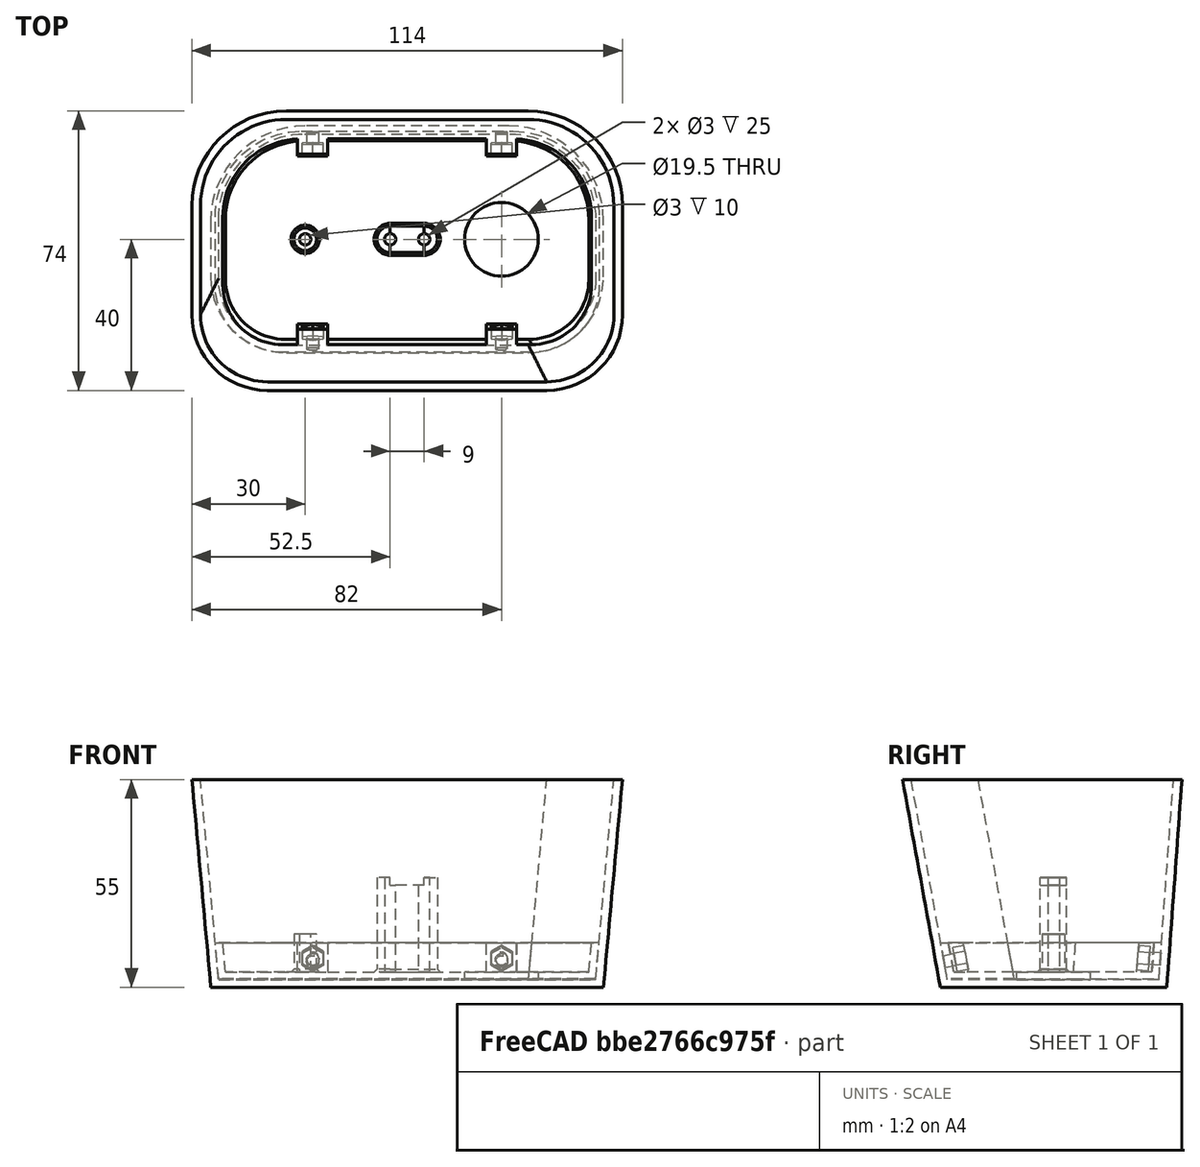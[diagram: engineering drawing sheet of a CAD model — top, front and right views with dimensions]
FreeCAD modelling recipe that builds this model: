
FCSTD DOCUMENT  (FreeCAD 0.19R22894 (Git))
Label: Rear_Cover_Plate
License: All rights reserved
LicenseURL: http://en.wikipedia.org/wiki/All_rights_reserved
objects: Sketcher::SketchObject×15, PartDesign::Pocket×7, PartDesign::Pad×4, PartDesign::AdditiveLoft×2, PartDesign::Thickness×2, PartDesign::Body×2, PartDesign::Chamfer×2, PartDesign::Boolean×1
note: 52 computed .brp shape members not serialized (recipe doc carries the construction recipe); baked Part::Feature solids carry a one-line shape summary decoded from their .brp

FEATURE [Sketcher::SketchObject] Sketch090
  MapMode = 5
  Support = -> [XY_Plane047]
  sketch-geometry (8):
    g0: LineSegment StartX=25 StartY=10 StartZ=0 EndX=89 EndY=10 EndZ=0
    g1: LineSegment StartX=109 StartY=30 StartZ=0 EndX=109 EndY=45 EndZ=0
    g2: LineSegment StartX=84 StartY=70 StartZ=0 EndX=30 EndY=70 EndZ=0
    g3: LineSegment StartX=5 StartY=45 StartZ=0 EndX=5 EndY=30 EndZ=0
    g4: ArcOfCircle CenterX=30 CenterY=45 CenterZ=0 NormalX=0 NormalY=0 NormalZ=1 AngleXU=0 Radius=25 StartAngle=1.5708 EndAngle=3.14159
    g5: ArcOfCircle CenterX=84 CenterY=45 CenterZ=0 NormalX=0 NormalY=0 NormalZ=1 AngleXU=0 Radius=25 StartAngle=0 EndAngle=1.5708
    g6: ArcOfCircle CenterX=89 CenterY=30 CenterZ=0 NormalX=0 NormalY=0 NormalZ=1 AngleXU=0 Radius=20 StartAngle=4.71239 EndAngle=6.28319
    g7: ArcOfCircle CenterX=25 CenterY=30 CenterZ=0 NormalX=0 NormalY=0 NormalZ=1 AngleXU=0 Radius=20 StartAngle=3.14159 EndAngle=4.71239
  constraints (20):
    c: Horizontal(g0)
    c: Horizontal(g2)
    c: Vertical(g1)
    c: Vertical(g3)
    c: Tangent(g3,g4) = -1.5708
    c: Tangent(g2,g4) = -1.5708
    c: Tangent(g2,g5) = -1.5708
    c: Tangent(g1,g5) = -1.5708
    c: Tangent(g1,g6) = -1.5708
    c: Tangent(g0,g6) = -1.5708
    c: Tangent(g0,g7) = -1.5708
    c: Tangent(g3,g7) = -1.5708
    c: Equal(g4,g5)
    c: Equal(g7,g6)
    c: Radius(g5) = 25
    c: Radius(g6) = 20
    c: DistanceY(g0,g2) = 60
    c: DistanceX(g3,g1) = 104
    c: DistanceY(g-1,g0) = 10
    c: DistanceX(g-1,g3) = 5
FEATURE [Sketcher::SketchObject] Sketch093
  AttachmentOffset = pos=(0,0,55) rot=(0,0,1;0rad)
  MapMode = 5
  Placement = pos=(0,0,55) rot=(0,0,1;0rad)
  Support = -> [XY_Plane048]
  sketch-geometry (8):
    g0: LineSegment StartX=25 StartY=74 StartZ=0 EndX=89 EndY=74 EndZ=0
    g1: LineSegment StartX=114 StartY=49 StartZ=0 EndX=114 EndY=20 EndZ=0
    g2: LineSegment StartX=94 StartY=0 StartZ=0 EndX=20 EndY=0 EndZ=0
    g3: LineSegment StartX=0 StartY=20 StartZ=0 EndX=0 EndY=49 EndZ=0
    g4: ArcOfCircle CenterX=20 CenterY=20 CenterZ=0 NormalX=0 NormalY=0 NormalZ=1 AngleXU=0 Radius=20 StartAngle=3.14159 EndAngle=4.71239
    g5: ArcOfCircle CenterX=25 CenterY=49 CenterZ=0 NormalX=0 NormalY=0 NormalZ=1 AngleXU=0 Radius=25 StartAngle=1.5708 EndAngle=3.14159
    g6: ArcOfCircle CenterX=89 CenterY=49 CenterZ=0 NormalX=0 NormalY=0 NormalZ=1 AngleXU=0 Radius=25 StartAngle=0 EndAngle=1.5708
    g7: ArcOfCircle CenterX=94 CenterY=20 CenterZ=0 NormalX=0 NormalY=0 NormalZ=1 AngleXU=0 Radius=20 StartAngle=4.71239 EndAngle=6.28319
  constraints (20):
    c: Horizontal(g0)
    c: Horizontal(g2)
    c: Vertical(g1)
    c: Vertical(g3)
    c: Tangent(g2,g4) = 1.5708
    c: Tangent(g3,g4) = 1.5708
    c: Tangent(g3,g5) = 1.5708
    c: Tangent(g0,g5) = 1.5708
    c: Tangent(g0,g6) = 1.5708
    c: Tangent(g1,g6) = 1.5708
    c: Tangent(g1,g7) = 1.5708
    c: Tangent(g2,g7) = 1.5708
    c: Equal(g4,g7)
    c: Equal(g5,g6)
    c: Radius(g6) = 25
    c: Radius(g7) = 20
    c: PointOnObject(g2,g-1)
    c: PointOnObject(g3,g-2)
    c: DistanceX(g3,g1) = 114
    c: DistanceY(g2,g0) = 74
FEATURE [Sketcher::SketchObject] Sketch094
  MapMode = 5
  Support = -> [XY_Plane048]
  sketch-geometry (8):
    g0: LineSegment StartX=25 StartY=10 StartZ=0 EndX=89 EndY=10 EndZ=0
    g1: LineSegment StartX=109 StartY=30 StartZ=0 EndX=109 EndY=45 EndZ=0
    g2: LineSegment StartX=84 StartY=70 StartZ=0 EndX=30 EndY=70 EndZ=0
    g3: LineSegment StartX=5 StartY=45 StartZ=0 EndX=5 EndY=30 EndZ=0
    g4: ArcOfCircle CenterX=30 CenterY=45 CenterZ=0 NormalX=0 NormalY=0 NormalZ=1 AngleXU=0 Radius=25 StartAngle=1.5708 EndAngle=3.14159
    g5: ArcOfCircle CenterX=84 CenterY=45 CenterZ=0 NormalX=0 NormalY=0 NormalZ=1 AngleXU=0 Radius=25 StartAngle=0 EndAngle=1.5708
    g6: ArcOfCircle CenterX=89 CenterY=30 CenterZ=0 NormalX=0 NormalY=0 NormalZ=1 AngleXU=0 Radius=20 StartAngle=4.71239 EndAngle=6.28319
    g7: ArcOfCircle CenterX=25 CenterY=30 CenterZ=0 NormalX=0 NormalY=0 NormalZ=1 AngleXU=0 Radius=20 StartAngle=3.14159 EndAngle=4.71239
  constraints (20):
    c: Horizontal(g0)
    c: Horizontal(g2)
    c: Vertical(g1)
    c: Vertical(g3)
    c: Tangent(g3,g4) = -1.5708
    c: Tangent(g2,g4) = -1.5708
    c: Tangent(g2,g5) = -1.5708
    c: Tangent(g1,g5) = -1.5708
    c: Tangent(g1,g6) = -1.5708
    c: Tangent(g0,g6) = -1.5708
    c: Tangent(g0,g7) = -1.5708
    c: Tangent(g3,g7) = -1.5708
    c: Equal(g4,g5)
    c: Equal(g7,g6)
    c: Radius(g5) = 25
    c: Radius(g6) = 20
    c: DistanceY(g0,g2) = 60
    c: DistanceX(g3,g1) = 104
    c: DistanceY(g-1,g0) = 10
    c: DistanceX(g-1,g3) = 5
FEATURE [PartDesign::AdditiveLoft] AdditiveLoft002  label="Baseplate001"
  AllowMultiFace = false
  Closed = false
  Profile = -> Sketch094
  Ruled = false
  Sections = -> [Sketch093]
FEATURE [PartDesign::Thickness] Thickness002  label="Make Shell"
  Base = -> AdditiveLoft002 [Face3]
  BaseFeature = -> AdditiveLoft002
  Intersection = false
  Join = 0
  Mode = 0
  Reversed = true
  SupportTransform = false
  Value = 2.25
FEATURE [PartDesign::Body] Body033  label="Rear_Cover_long"
  Group = -> [Sketch093,Sketch094,AdditiveLoft002,Thickness002]
  Origin = -> Origin049
  Tip = -> Thickness002
FEATURE [Sketcher::SketchObject] Sketch092
  AttachmentOffset = pos=(0,0,55) rot=(0,0,1;0rad)
  MapMode = 5
  Placement = pos=(0,0,55) rot=(0,0,1;0rad)
  Support = -> [XY_Plane047]
  sketch-geometry (8):
    g0: LineSegment StartX=25 StartY=74 StartZ=0 EndX=89 EndY=74 EndZ=0
    g1: LineSegment StartX=114 StartY=49 StartZ=0 EndX=114 EndY=20 EndZ=0
    g2: LineSegment StartX=94 StartY=0 StartZ=0 EndX=20 EndY=0 EndZ=0
    g3: LineSegment StartX=0 StartY=20 StartZ=0 EndX=0 EndY=49 EndZ=0
    g4: ArcOfCircle CenterX=20 CenterY=20 CenterZ=0 NormalX=0 NormalY=0 NormalZ=1 AngleXU=0 Radius=20 StartAngle=3.14159 EndAngle=4.71239
    g5: ArcOfCircle CenterX=25 CenterY=49 CenterZ=0 NormalX=0 NormalY=0 NormalZ=1 AngleXU=0 Radius=25 StartAngle=1.5708 EndAngle=3.14159
    g6: ArcOfCircle CenterX=89 CenterY=49 CenterZ=0 NormalX=0 NormalY=0 NormalZ=1 AngleXU=0 Radius=25 StartAngle=0 EndAngle=1.5708
    g7: ArcOfCircle CenterX=94 CenterY=20 CenterZ=0 NormalX=0 NormalY=0 NormalZ=1 AngleXU=0 Radius=20 StartAngle=4.71239 EndAngle=6.28319
  constraints (20):
    c: Horizontal(g0)
    c: Horizontal(g2)
    c: Vertical(g1)
    c: Vertical(g3)
    c: Tangent(g2,g4) = 1.5708
    c: Tangent(g3,g4) = 1.5708
    c: Tangent(g3,g5) = 1.5708
    c: Tangent(g0,g5) = 1.5708
    c: Tangent(g0,g6) = 1.5708
    c: Tangent(g1,g6) = 1.5708
    c: Tangent(g1,g7) = 1.5708
    c: Tangent(g2,g7) = 1.5708
    c: Equal(g4,g7)
    c: Equal(g5,g6)
    c: Radius(g6) = 25
    c: Radius(g7) = 20
    c: PointOnObject(g2,g-1)
    c: PointOnObject(g3,g-2)
    c: DistanceX(g3,g1) = 114
    c: DistanceY(g2,g0) = 74
FEATURE [PartDesign::AdditiveLoft] AdditiveLoft001  label="Baseplate"
  AllowMultiFace = false
  Closed = false
  Profile = -> Sketch090
  Ruled = false
  Sections = -> [Sketch092]
FEATURE [PartDesign::Thickness] Thickness001  label="Make Thick Shell"
  Base = -> AdditiveLoft001 [Face3]
  BaseFeature = -> AdditiveLoft001
  Intersection = false
  Join = 0
  Mode = 0
  Reversed = true
  SupportTransform = false
  Value = 4.25
FEATURE [PartDesign::Boolean] Boolean
  BaseFeature = -> Thickness001
  Group = -> [Body033]
  Type = 1
FEATURE [Sketcher::SketchObject] Sketch095
  MapMode = 5
  Placement = pos=(0,0,55) rot=(0,0,1;0rad)
  Support = -> [Boolean]
  sketch-geometry (4):
    g0: LineSegment StartX=0 StartY=0 StartZ=0 EndX=118 EndY=0 EndZ=0
    g1: LineSegment StartX=118 StartY=0 StartZ=0 EndX=118 EndY=75 EndZ=0
    g2: LineSegment StartX=118 StartY=75 StartZ=0 EndX=0 EndY=75 EndZ=0
    g3: LineSegment StartX=0 StartY=75 StartZ=0 EndX=0 EndY=0 EndZ=0
  constraints (11):
    c: Coincident(g0,g1)
    c: Coincident(g1,g2)
    c: Coincident(g2,g3)
    c: Coincident(g3,g0)
    c: Horizontal(g0)
    c: Horizontal(g2)
    c: Vertical(g1)
    c: Vertical(g3)
    c: Coincident(g0,g-1)
    c: DistanceX(g2,g2) = 118
    c: DistanceY(g1,g1) = 75
FEATURE [PartDesign::Pocket] Pocket033  label="Shorten Shell"
  AllowMultiFace = false
  BaseFeature = -> Boolean
  Length = 43
  Length2 = 100
  Profile = -> Sketch095
  Type = 0
FEATURE [Sketcher::SketchObject] Sketch254
  AttachmentOffset = pos=(0,0,32) rot=(0,0,1;0rad)
  ExternalGeometry = -> [Pocket033]
  MapMode = 5
  Placement = pos=(32,-7.1e-15,7.1e-15) rot=(0.57735,0.57735,0.57735;2.0944rad)
  Support = -> [YZ_Plane047]
  sketch-geometry (8):
    g0: LineSegment StartX=12.1379 StartY=12 StartZ=0 EndX=13.5469 EndY=4.25 EndZ=0
    g1: LineSegment StartX=13.5469 StartY=4.25 StartZ=0 EndX=17.5469 EndY=4.25 EndZ=0
    g2: LineSegment StartX=17.5469 StartY=4.25 StartZ=0 EndX=16.1379 EndY=12 EndZ=0
    g3: LineSegment StartX=16.1379 StartY=12 StartZ=0 EndX=12.1379 EndY=12 EndZ=0
    g4: LineSegment StartX=66.0479 StartY=4.25 StartZ=0 EndX=62.0479 EndY=4.25 EndZ=0
    g5: LineSegment StartX=62.0479 StartY=4.25 StartZ=0 EndX=62.6115 EndY=12 EndZ=0
    g6: LineSegment StartX=62.6115 StartY=12 StartZ=0 EndX=66.6115 EndY=12 EndZ=0
    g7: LineSegment StartX=66.6115 StartY=12 StartZ=0 EndX=66.0479 EndY=4.25 EndZ=0
  constraints (20):
    c: Coincident(g0,g-3)
    c: Coincident(g0,g-3)
    c: Coincident(g0,g1)
    c: Horizontal(g1)
    c: Coincident(g1,g2)
    c: Coincident(g2,g3)
    c: Horizontal(g3)
    c: Coincident(g3,g0)
    c: Parallel(g2,g0)
    c: DistanceX(g3,g3) = 4
    c: Horizontal(g4)
    c: Coincident(g4,g5)
    c: Coincident(g5,g6)
    c: Coincident(g6,g-4)
    c: Horizontal(g6)
    c: Coincident(g6,g7)
    c: Coincident(g7,g4)
    c: Parallel(g7,g5)
    c: Coincident(g4,g-4)
    c: DistanceX(g6,g6) = 4
FEATURE [PartDesign::Pad] Pad112  label="Add Screwpads right"
  AllowMultiFace = false
  BaseFeature = -> Pocket033
  Direction = (1,1,1)
  Length = 4
  Length2 = 4
  Profile = -> Sketch254
  Type = 4
FEATURE [Sketcher::SketchObject] Sketch255
  AttachmentOffset = pos=(0,0,82) rot=(0,0,1;0rad)
  ExternalGeometry = -> [Pocket033]
  MapMode = 5
  Placement = pos=(82,-1.82e-14,1.82e-14) rot=(0.57735,0.57735,0.57735;2.0944rad)
  Support = -> [YZ_Plane047]
  sketch-geometry (8):
    g0: LineSegment StartX=12.1379 StartY=12 StartZ=0 EndX=13.5469 EndY=4.25 EndZ=0
    g1: LineSegment StartX=13.5469 StartY=4.25 StartZ=0 EndX=17.5469 EndY=4.25 EndZ=0
    g2: LineSegment StartX=17.5469 StartY=4.25 StartZ=0 EndX=16.1379 EndY=12 EndZ=0
    g3: LineSegment StartX=16.1379 StartY=12 StartZ=0 EndX=12.1379 EndY=12 EndZ=0
    g4: LineSegment StartX=66.0479 StartY=4.25 StartZ=0 EndX=62.0479 EndY=4.25 EndZ=0
    g5: LineSegment StartX=62.0479 StartY=4.25 StartZ=0 EndX=62.6115 EndY=12 EndZ=0
    g6: LineSegment StartX=62.6115 StartY=12 StartZ=0 EndX=66.6115 EndY=12 EndZ=0
    g7: LineSegment StartX=66.6115 StartY=12 StartZ=0 EndX=66.0479 EndY=4.25 EndZ=0
  constraints (20):
    c: Coincident(g0,g-3)
    c: Coincident(g0,g-3)
    c: Coincident(g0,g1)
    c: Horizontal(g1)
    c: Coincident(g1,g2)
    c: Coincident(g2,g3)
    c: Horizontal(g3)
    c: Coincident(g3,g0)
    c: Parallel(g2,g0)
    c: DistanceX(g3,g3) = 4
    c: Horizontal(g4)
    c: Coincident(g4,g5)
    c: Coincident(g5,g6)
    c: Coincident(g6,g-4)
    c: Horizontal(g6)
    c: Coincident(g6,g7)
    c: Coincident(g7,g4)
    c: Parallel(g7,g5)
    c: Coincident(g4,g-4)
    c: DistanceX(g6,g6) = 4
FEATURE [PartDesign::Pad] Pad113  label="Add Screwpads left"
  AllowMultiFace = false
  BaseFeature = -> Pad112
  Direction = (1,1,1)
  Length = 4
  Length2 = 4
  Profile = -> Sketch255
  Type = 4
FEATURE [Sketcher::SketchObject] Sketch256
  ExternalGeometry = -> [Pad113]
  MapMode = 5
  Placement = pos=(3e-15,17.7334,3.22426) rot=(0,0.640747,0.767752;3.14159rad)
  Support = -> [Pad113]
  sketch-geometry (5):
    g0: Circle CenterX=-82 CenterY=4.98108 CenterZ=0 NormalX=0 NormalY=0 NormalZ=1 AngleXU=0 Radius=1.6
    g1: Circle CenterX=-32 CenterY=4.98108 CenterZ=0 NormalX=0 NormalY=0 NormalZ=1 AngleXU=0 Radius=1.6
    g2: LineSegment [constr] StartX=-86 StartY=8.91961 StartZ=0 EndX=-82 EndY=4.98108 EndZ=0
    g3: LineSegment [constr] StartX=-82 StartY=4.98108 StartZ=0 EndX=-78 EndY=8.91961 EndZ=0
    g4: LineSegment [constr] StartX=-78 StartY=1.04255 StartZ=0 EndX=-82 EndY=4.98108 EndZ=0
  constraints (12):
    c: Equal(g1,g0)
    c: Radius(g0) = 1.6
    c: Horizontal(g0,g1)
    c: DistanceX(g0,g1) = 50
    c: Coincident(g2,g-3)
    c: Coincident(g2,g0)
    c: Coincident(g3,g0)
    c: Coincident(g3,g-3)
    c: Equal(g2,g3)
    c: Coincident(g4,g-4)
    c: Coincident(g4,g0)
    c: Equal(g4,g3)
FEATURE [PartDesign::Pocket] Pocket115  label="Add Screwholes top"
  AllowMultiFace = false
  BaseFeature = -> Pad113
  Length = 10
  Length2 = 100
  Profile = -> Sketch256
  Type = 0
FEATURE [Sketcher::SketchObject] Sketch257
  ExternalGeometry = -> [Pocket115]
  MapMode = 5
  Placement = pos=(3e-15,17.7334,3.22426) rot=(0,0.640747,0.767752;3.14159rad)
  Support = -> [Pocket115]
  sketch-geometry (14):
    g0: LineSegment StartX=-82 StartY=8.21424 StartZ=0 EndX=-84.8 EndY=6.59766 EndZ=0
    g1: LineSegment StartX=-84.8 StartY=6.59766 StartZ=0 EndX=-84.8 EndY=3.3645 EndZ=0
    g2: LineSegment StartX=-84.8 StartY=3.3645 StartZ=0 EndX=-82 EndY=1.74792 EndZ=0
    g3: LineSegment StartX=-82 StartY=1.74792 StartZ=0 EndX=-79.2 EndY=3.3645 EndZ=0
    g4: LineSegment StartX=-79.2 StartY=3.3645 StartZ=0 EndX=-79.2 EndY=6.59766 EndZ=0
    g5: LineSegment StartX=-79.2 StartY=6.59766 StartZ=0 EndX=-82 EndY=8.21424 EndZ=0
    g6: Circle [constr] CenterX=-82 CenterY=4.98108 CenterZ=0 NormalX=0 NormalY=0 NormalZ=1 AngleXU=0 Radius=3.23316
    g7: LineSegment StartX=-32 StartY=8.21424 StartZ=0 EndX=-34.8 EndY=6.59766 EndZ=0
    g8: LineSegment StartX=-34.8 StartY=6.59766 StartZ=0 EndX=-34.8 EndY=3.3645 EndZ=0
    g9: LineSegment StartX=-34.8 StartY=3.3645 StartZ=0 EndX=-32 EndY=1.74792 EndZ=0
    g10: LineSegment StartX=-32 StartY=1.74792 StartZ=0 EndX=-29.2 EndY=3.3645 EndZ=0
    g11: LineSegment StartX=-29.2 StartY=3.3645 StartZ=0 EndX=-29.2 EndY=6.59766 EndZ=0
    g12: LineSegment StartX=-29.2 StartY=6.59766 StartZ=0 EndX=-32 EndY=8.21424 EndZ=0
    g13: Circle [constr] CenterX=-32 CenterY=4.98108 CenterZ=0 NormalX=0 NormalY=0 NormalZ=1 AngleXU=0 Radius=3.23316
  constraints (33):
    c: Coincident(g0,g1)
    c: Coincident(g1,g2)
    c: Coincident(g2,g3)
    c: Coincident(g3,g4)
    c: Coincident(g4,g5)
    c: Coincident(g5,g0)
    c: Equal(g0, g1-g5) x5
    c: PointOnObject(g0,g6)
    c: PointOnObject(g1,g6)
    c: PointOnObject(g2,g6)
    c: PointOnObject(g3,g6)
    c: PointOnObject(g4,g6)
    c: PointOnObject(g5,g6)
    c: Coincident(g7,g8)
    c: Coincident(g8,g9)
    c: Coincident(g9,g10)
    c: Coincident(g10,g11)
    c: Coincident(g11,g12)
    c: Coincident(g12,g7)
    c: Equal(g7, g8-g12) x5
    c: PointOnObject(g7,g13)
    c: PointOnObject(g8,g13)
    c: PointOnObject(g9,g13)
    c: PointOnObject(g10,g13)
    c: PointOnObject(g11,g13)
    c: PointOnObject(g12,g13)
    c: Coincident(g6,g-3)
    c: Vertical(g1)
    c: Vertical(g8)
    c: Equal(g6,g13)
    c: DistanceX(g0,g4) = 5.6
    c: Horizontal(g13,g6)
    c: DistanceX(g6,g13) = 50
FEATURE [PartDesign::Pocket] Pocket116  label="Add Screwholes bottom"
  AllowMultiFace = false
  BaseFeature = -> Pocket115
  Length = 3
  Length2 = 100
  Profile = -> Sketch257
  Type = 0
FEATURE [Sketcher::SketchObject] Sketch258
  ExternalGeometry = -> [Pocket116]
  MapMode = 5
  Placement = pos=(1.49e-14,61.4139,-4.46647) rot=(1,0,0;1.4982rad)
  Support = -> [Pocket116]
  sketch-geometry (5):
    g0: Circle CenterX=32 CenterY=12.6247 CenterZ=0 NormalX=0 NormalY=0 NormalZ=1 AngleXU=0 Radius=1.6
    g1: Circle CenterX=82 CenterY=12.6247 CenterZ=0 NormalX=0 NormalY=0 NormalZ=1 AngleXU=0 Radius=1.6
    g2: LineSegment [constr] StartX=28 StartY=16.51 StartZ=0 EndX=32 EndY=12.6247 EndZ=0
    g3: LineSegment [constr] StartX=32 StartY=12.6247 StartZ=0 EndX=36 EndY=16.51 EndZ=0
    g4: LineSegment [constr] StartX=32 StartY=12.6247 StartZ=0 EndX=36 EndY=8.73949 EndZ=0
  constraints (12):
    c: Horizontal(g0,g1)
    c: Equal(g1,g0)
    c: DistanceX(g0,g1) = 50
    c: Coincident(g2,g-3)
    c: Coincident(g2,g0)
    c: Coincident(g3,g0)
    c: Coincident(g3,g-3)
    c: Coincident(g4,g0)
    c: Coincident(g4,g-4)
    c: Equal(g2,g3)
    c: Equal(g3,g4)
    c: Radius(g0) = 1.6
FEATURE [PartDesign::Pocket] Pocket117  label="Add Nutpockets top"
  AllowMultiFace = false
  BaseFeature = -> Pocket116
  Length = 10
  Length2 = 100
  Profile = -> Sketch258
  Type = 0
FEATURE [Sketcher::SketchObject] Sketch259
  ExternalGeometry = -> [Pocket117]
  MapMode = 5
  Placement = pos=(1.49e-14,61.4139,-4.46647) rot=(1,0,0;1.4982rad)
  Support = -> [Pocket117]
  sketch-geometry (14):
    g0: LineSegment StartX=32 StartY=15.8579 StartZ=0 EndX=29.2 EndY=14.2413 EndZ=0
    g1: LineSegment StartX=29.2 StartY=14.2413 StartZ=0 EndX=29.2 EndY=11.0081 EndZ=0
    g2: LineSegment StartX=29.2 StartY=11.0081 StartZ=0 EndX=32 EndY=9.39156 EndZ=0
    g3: LineSegment StartX=32 StartY=9.39156 StartZ=0 EndX=34.8 EndY=11.0081 EndZ=0
    g4: LineSegment StartX=34.8 StartY=11.0081 StartZ=0 EndX=34.8 EndY=14.2413 EndZ=0
    g5: LineSegment StartX=34.8 StartY=14.2413 StartZ=0 EndX=32 EndY=15.8579 EndZ=0
    g6: Circle [constr] CenterX=32 CenterY=12.6247 CenterZ=0 NormalX=0 NormalY=0 NormalZ=1 AngleXU=0 Radius=3.23316
    g7: LineSegment StartX=82 StartY=15.8579 StartZ=0 EndX=79.2 EndY=14.2413 EndZ=0
    g8: LineSegment StartX=79.2 StartY=14.2413 StartZ=0 EndX=79.2 EndY=11.0081 EndZ=0
    g9: LineSegment StartX=79.2 StartY=11.0081 StartZ=0 EndX=82 EndY=9.39156 EndZ=0
    g10: LineSegment StartX=82 StartY=9.39156 StartZ=0 EndX=84.8 EndY=11.0081 EndZ=0
    g11: LineSegment StartX=84.8 StartY=11.0081 StartZ=0 EndX=84.8 EndY=14.2413 EndZ=0
    g12: LineSegment StartX=84.8 StartY=14.2413 StartZ=0 EndX=82 EndY=15.8579 EndZ=0
    g13: Circle [constr] CenterX=82 CenterY=12.6247 CenterZ=0 NormalX=0 NormalY=0 NormalZ=1 AngleXU=0 Radius=3.23316
  constraints (33):
    c: Coincident(g0,g1)
    c: Coincident(g1,g2)
    c: Coincident(g2,g3)
    c: Coincident(g3,g4)
    c: Coincident(g4,g5)
    c: Coincident(g5,g0)
    c: Equal(g0, g1-g5) x5
    c: PointOnObject(g0,g6)
    c: PointOnObject(g1,g6)
    c: PointOnObject(g2,g6)
    c: PointOnObject(g3,g6)
    c: PointOnObject(g4,g6)
    c: PointOnObject(g5,g6)
    c: Coincident(g7,g8)
    c: Coincident(g8,g9)
    c: Coincident(g9,g10)
    c: Coincident(g10,g11)
    c: Coincident(g11,g12)
    c: Coincident(g12,g7)
    c: Equal(g7, g8-g12) x5
    c: PointOnObject(g7,g13)
    c: PointOnObject(g8,g13)
    c: PointOnObject(g9,g13)
    c: PointOnObject(g10,g13)
    c: PointOnObject(g11,g13)
    c: PointOnObject(g12,g13)
    c: Vertical(g4)
    c: Vertical(g8)
    c: Equal(g13,g6)
    c: Coincident(g-3,g6)
    c: Horizontal(g6,g13)
    c: DistanceX(g6,g13) = 50
    c: DistanceX(g0,g4) = 5.6
FEATURE [PartDesign::Pocket] Pocket118  label="Add Nutpockets bottom"
  AllowMultiFace = false
  BaseFeature = -> Pocket117
  Length = 3
  Length2 = 100
  Profile = -> Sketch259
  Type = 0
FEATURE [Sketcher::SketchObject] Sketch660
  MapMode = 5
  Placement = pos=(0,0,4.25) rot=(0,0,1;0rad)
  Support = -> [Pocket118]
  sketch-geometry (2):
    g0: Circle CenterX=30 CenterY=40 CenterZ=0 NormalX=0 NormalY=0 NormalZ=1 AngleXU=0 Radius=3
    g1: Circle CenterX=30 CenterY=40 CenterZ=0 NormalX=0 NormalY=0 NormalZ=1 AngleXU=0 Radius=1.5
  constraints (5):
    c: Coincident(g1,g0)
    c: Radius(g1) = 1.5
    c: Radius(g0) = 3
    c: DistanceX(g-1,g0) = 30
    c: DistanceY(g-1,g0) = 40
FEATURE [PartDesign::Pad] Pad329  label="Add Voltage Sensor Mountingpin"
  AllowMultiFace = false
  BaseFeature = -> Pocket118
  Direction = (1,1,1)
  Length = 10
  Length2 = 100
  Profile = -> Sketch660
  Type = 0
FEATURE [Sketcher::SketchObject] Sketch661
  MapMode = 5
  Placement = pos=(0,0,4.25) rot=(0,0,1;0rad)
  Support = -> [Pad329]
  sketch-geometry (6):
    g0: ArcOfCircle CenterX=52.5 CenterY=40 CenterZ=0 NormalX=0 NormalY=0 NormalZ=1 AngleXU=0 Radius=3.5 StartAngle=1.5708 EndAngle=4.71239
    g1: ArcOfCircle CenterX=61.5 CenterY=40 CenterZ=0 NormalX=0 NormalY=0 NormalZ=1 AngleXU=0 Radius=3.5 StartAngle=4.71239 EndAngle=7.85398
    g2: LineSegment StartX=52.5 StartY=36.5 StartZ=0 EndX=61.5 EndY=36.5 EndZ=0
    g3: LineSegment StartX=52.5 StartY=43.5 StartZ=0 EndX=61.5 EndY=43.5 EndZ=0
    g4: Circle CenterX=52.5 CenterY=40 CenterZ=0 NormalX=0 NormalY=0 NormalZ=1 AngleXU=0 Radius=1.5
    g5: Circle CenterX=61.5 CenterY=40 CenterZ=0 NormalX=0 NormalY=0 NormalZ=1 AngleXU=0 Radius=1.5
  constraints (14):
    c: Tangent(g0,g3) = 1.5708
    c: Tangent(g0,g2) = -1.5708
    c: Tangent(g2,g1) = -1.5708
    c: Tangent(g3,g1) = 1.5708
    c: Horizontal(g2)
    c: Equal(g0,g1)
    c: Coincident(g4,g0)
    c: Coincident(g1,g5)
    c: Equal(g4,g5)
    c: Radius(g5) = 1.5
    c: Radius(g1) = 3.5
    c: DistanceX(g0,g1) = 9
    c: DistanceY(g-1,g0) = 40
    c: DistanceX(g-1,g0) = 52.5
FEATURE [PartDesign::Pad] Pad330  label="Add Current Sensor Mountingpin"
  AllowMultiFace = false
  BaseFeature = -> Pad329
  Direction = (1,1,1)
  Length = 25
  Length2 = 100
  Profile = -> Sketch661
  Type = 0
FEATURE [Sketcher::SketchObject] Sketch663
  AttachmentOffset = pos=(0,0,3) rot=(0,0,1;0rad)
  MapMode = 5
  Placement = pos=(0,0,5) rot=(0,0,1;0rad)
  sketch-geometry (1):
    g0: Circle CenterX=82 CenterY=40 CenterZ=0 NormalX=0 NormalY=0 NormalZ=1 AngleXU=0 Radius=9.75
  constraints (3):
    c: Radius(g0) = 9.75
    c: DistanceX(g-1,g0) = 82
    c: DistanceY(g-1,g0) = 40
FEATURE [PartDesign::Chamfer] Chamfer  label="Fortify Current Sensor Mountingpin"
  Angle = 45
  Base = -> Pad330 [Edge119]
  BaseFeature = -> Pad330
  ChamferType = 0
  FlipDirection = false
  Size = 0.75
  Size2 = 1
  SupportTransform = false
FEATURE [PartDesign::Chamfer] Chamfer104  label="Fortify Voltage Sensor Mountingpin"
  Angle = 45
  Base = -> Chamfer [Edge27]
  BaseFeature = -> Chamfer
  ChamferType = 0
  FlipDirection = false
  Size = 0.75
  Size2 = 1
  SupportTransform = false
FEATURE [Sketcher::SketchObject] Sketch662
  ExternalGeometry = -> [Chamfer104]
  MapMode = 5
  Placement = pos=(0,36.5,0) rot=(1,0,0;1.5708rad)
  Support = -> [Chamfer104]
  sketch-geometry (4):
    g0: LineSegment StartX=52.5 StartY=29.25 StartZ=0 EndX=61.5 EndY=29.25 EndZ=0
    g1: LineSegment StartX=61.5 StartY=29.25 StartZ=0 EndX=61.5 EndY=27.25 EndZ=0
    g2: LineSegment StartX=61.5 StartY=27.25 StartZ=0 EndX=52.5 EndY=27.25 EndZ=0
    g3: LineSegment StartX=52.5 StartY=27.25 StartZ=0 EndX=52.5 EndY=29.25 EndZ=0
  constraints (10):
    c: Coincident(g0,g1)
    c: Coincident(g1,g2)
    c: Coincident(g2,g3)
    c: Coincident(g3,g0)
    c: Horizontal(g2)
    c: Vertical(g1)
    c: Vertical(g3)
    c: Coincident(g0,g-3)
    c: Coincident(g0,g-4)
    c: DistanceY(g3,g3) = 2
FEATURE [PartDesign::Pocket] Pocket338  label="Cutout for Current Sensor IC"
  AllowMultiFace = false
  BaseFeature = -> Chamfer104
  Length = 8
  Length2 = 100
  Profile = -> Sketch662
  Type = 0
FEATURE [PartDesign::Pocket] Pocket339  label="Pushbutton Hole 19mm"
  AllowMultiFace = false
  BaseFeature = -> Pocket338
  Length = 5
  Length2 = 100
  Profile = -> Sketch663
  Type = 0
FEATURE [PartDesign::Body] Body032  label="Rear_Cover_Plate"
  Group = -> [Sketch092,Sketch090,AdditiveLoft001,Thickness001,Boolean,Sketch095,Pocket033,Sketch254,Pad112,Sketch255,Pad113,Sketch256,Pocket115,Sketch257,Pocket116,Sketch258,Pocket117,Sketch259,Pocket118,Sketch660,Pad329,Sketch661,Pad330,Chamfer,Chamfer104,Sketch662,Pocket338,Sketch663,Pocket339]
  Origin = -> Origin048
  Placement = pos=(0,0,-0.25) rot=(0,0,1;0rad)
  Tip = -> Pocket339
